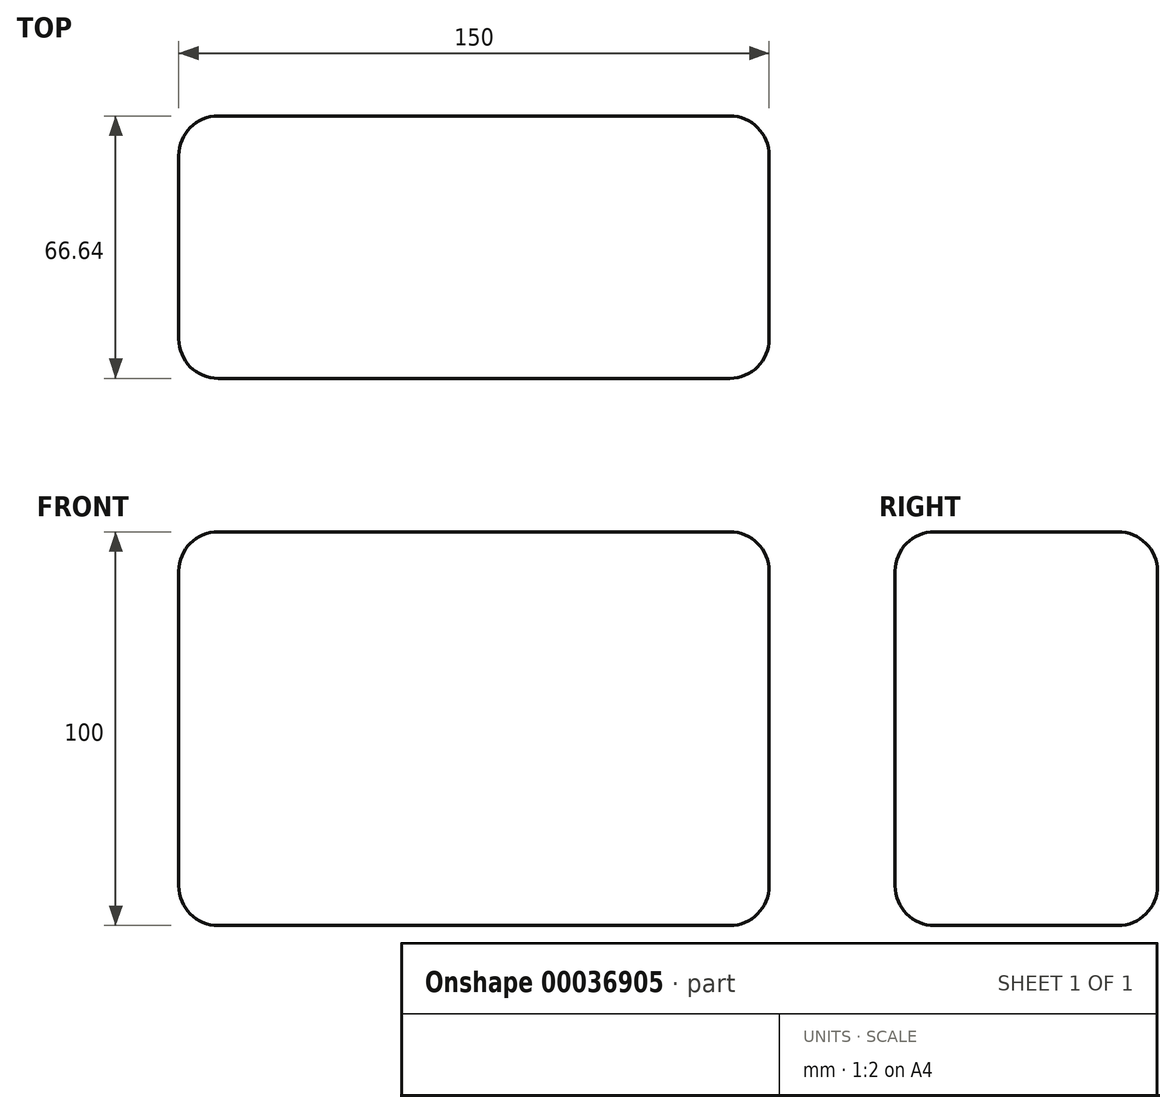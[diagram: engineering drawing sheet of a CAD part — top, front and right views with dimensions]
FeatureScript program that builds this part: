
annotation { "Feature Type Name" : "Feature", "Feature Type Description" : "" }
export const myFeature = defineFeature(function(context is Context, id is Id, definition is map)
    precondition{}
    {
        {
            var Q0;
            Q0=qCreatedBy(makeId("Top.planeOp"),FACE);
            var sketch = newSketch(context, id + "F0", { "sketchPlane" : qUnion([Q0])});
            skLineSegment(sketch, "E0.bottom", {"start": v(-75, 35.38) * mm, "end": v(75, 35.38) * mm});
            skLineSegment(sketch, "E0.top", {"start": v(-75, -31.26) * mm, "end": v(75, -31.26) * mm});
            skLineSegment(sketch, "E0.left", {"start": v(-75, 35.38) * mm, "end": v(-75, -31.26) * mm});
            skLineSegment(sketch, "E0.right", {"start": v(75, 35.38) * mm, "end": v(75, -31.26) * mm});
            skLineSegment(sketch, "E1.left", {"start": v(-75, 35.38) * mm, "end": v(-75, 35.38) * mm});
            skLineSegment(sketch, "E1.right", {"start": v(75, 35.38) * mm, "end": v(75, 35.38) * mm});
            skSolve(sketch);
        }
        {
            var Q0;
            Q0 = qSketchRegion(id + "F0", true);
            extrude(context, id + "F1", {"entities" : qUnion([Q0]), "depth" : 100 * mm});
        }
        {
            var Q0;
            Q0=makeQuery(id+"F1.opExtrude","SWEPT_FACE",FACE,{"disambiguationData":[OSD([sQuery(id+"F0.wireOp",EDGE,"E0.bottom")])]});
            var Q1;
            Q1=makeQuery(id+"F1.opExtrude","SWEPT_FACE",FACE,{"disambiguationData":[OSD([sQuery(id+"F0.wireOp",EDGE,"E0.top")])]});
            var Q2;
            Q2=makeQuery(id+"F1.opExtrude","SWEPT_FACE",FACE,{"disambiguationData":[OSD([sQuery(id+"F0.wireOp",EDGE,"E0.left")])]});
            var Q3;
            Q3=makeQuery(id+"F1.opExtrude","CAP_FACE",FACE,{"disambiguationData":[OSD([sQuery(id+"F0.wireOp",EDGE,"E0.top"),sQuery(id+"F0.wireOp",EDGE,"E0.left"),sQuery(id+"F0.wireOp",EDGE,"E0.right"),sQuery(id+"F0.wireOp",EDGE,"E0.bottom")])],"isStart":true});
            var Q4;
            Q4=makeQuery(id+"F1.opExtrude","CAP_FACE",FACE,{"disambiguationData":[OSD([sQuery(id+"F0.wireOp",EDGE,"E0.top"),sQuery(id+"F0.wireOp",EDGE,"E0.left"),sQuery(id+"F0.wireOp",EDGE,"E0.right"),sQuery(id+"F0.wireOp",EDGE,"E0.bottom")])],"isStart":false});
            fillet(context, id + "F2", {"entities" : qUnion([Q0, Q1, Q2, Q3, Q4]), "radius" : 10 * mm, "tangentPropagation" : true, "allowEdgeOverflow" : false});
        }
    });
